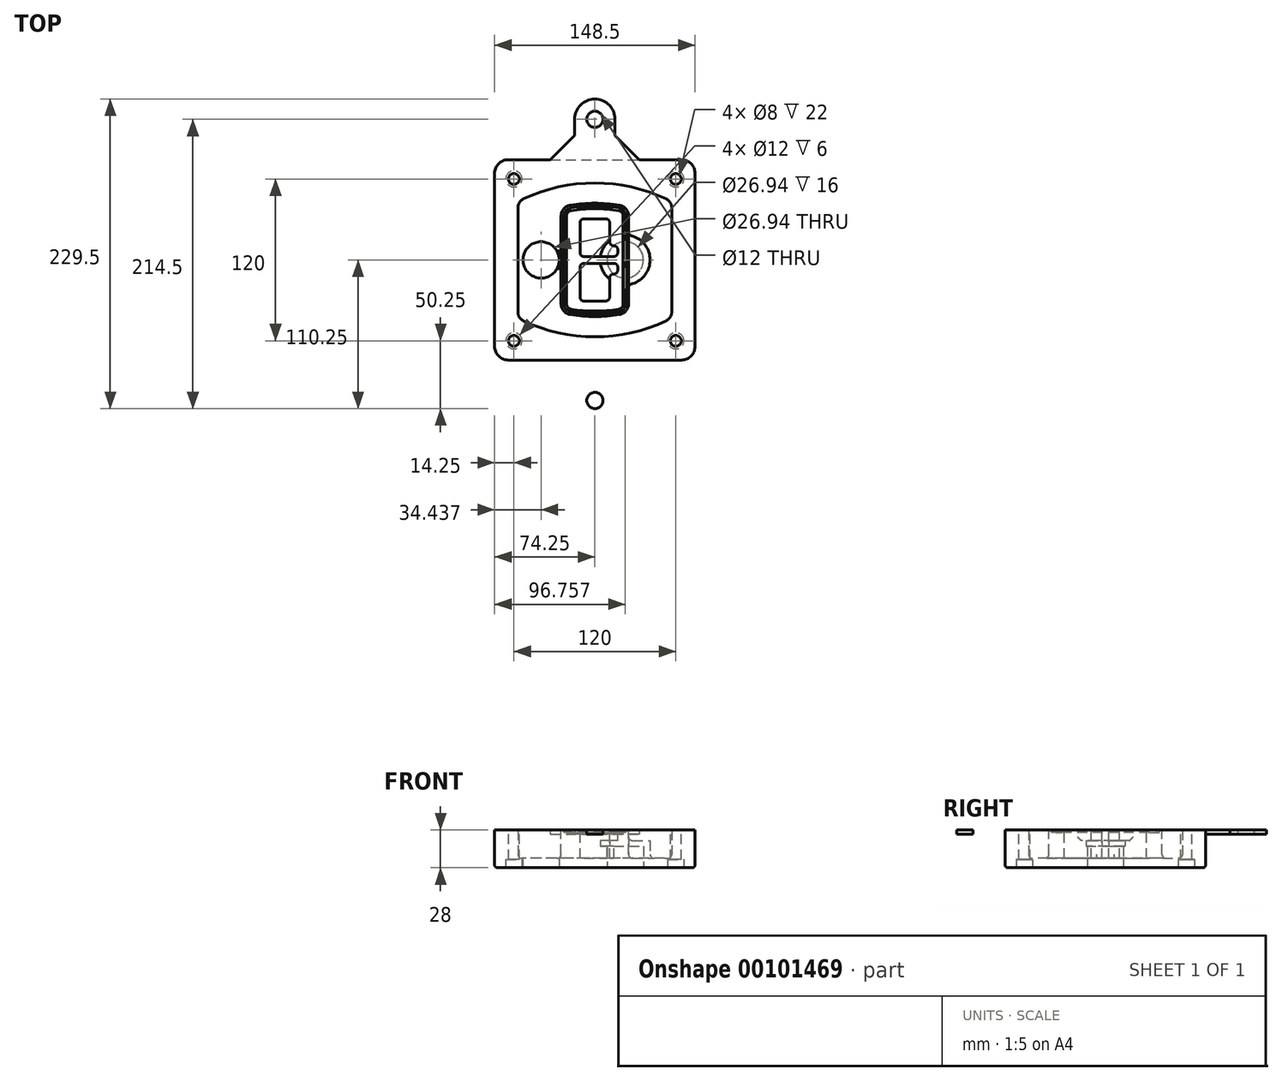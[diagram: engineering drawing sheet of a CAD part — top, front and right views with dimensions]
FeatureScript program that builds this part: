
annotation { "Feature Type Name" : "Feature", "Feature Type Description" : "" }
export const myFeature = defineFeature(function(context is Context, id is Id, definition is map)
    precondition{}
    {
        {
            var Q0;
            Q0=qCreatedBy(makeId("Top.planeOp"),FACE);
            var sketch = newSketch(context, id + "F0", { "sketchPlane" : qUnion([Q0])});
            skPoint(sketch, "E0.rect.middle", {"position": v(0, 0) * mm});
            skLineSegment(sketch, "E1.bottom", {"start": v(-64.25, -74.25) * mm, "end": v(64.25, -74.25) * mm});
            skLineSegment(sketch, "E1.top", {"start": v(-64.25, 74.25) * mm, "end": v(64.25, 74.25) * mm});
            skLineSegment(sketch, "E1.left", {"start": v(-74.25, -64.25) * mm, "end": v(-74.25, 64.25) * mm});
            skLineSegment(sketch, "E1.right", {"start": v(74.25, -64.25) * mm, "end": v(74.25, 64.25) * mm});
            skLineSegment(sketch, "E2", {"start": v(-74.25, 74.25) * mm, "end": v(74.25, -74.25) * mm, "construction": true});
            skLineSegment(sketch, "E3", {"start": v(74.25, 74.25) * mm, "end": v(-74.25, -74.25) * mm, "construction": true});
            skCircle(sketch, "E4", {"center": v(-60, 60) * mm, "radius": 4 * mm});
            skCircle(sketch, "E5", {"center": v(60, 60) * mm, "radius": 4 * mm});
            skCircle(sketch, "E6", {"center": v(60, -60) * mm, "radius": 4 * mm});
            skCircle(sketch, "E7", {"center": v(-60, -60) * mm, "radius": 4 * mm});
            skLineSegment(sketch, "E8", {"start": v(-60, 60) * mm, "end": v(60, 60) * mm, "construction": true});
            skLineSegment(sketch, "E9", {"start": v(60, 60) * mm, "end": v(60, -60) * mm, "construction": true});
            skLineSegment(sketch, "E10", {"start": v(60, -60) * mm, "end": v(-60, -60) * mm, "construction": true});
            skLineSegment(sketch, "E11", {"start": v(-60, -60) * mm, "end": v(-60, 60) * mm, "construction": true});
            skLineSegment(sketch, "E12", {"start": v(-60, 38.83) * mm, "end": v(-60, -38.83) * mm});
            skLineSegment(sketch, "E13", {"start": v(60, 38.83) * mm, "end": v(60, -38.83) * mm});
            skArc(sketch, "E14", {"start": v(54.26, 47.88) * mm, "mid": v(0, 60) * mm, "end": v(-54.26, 47.88) * mm});
            skArc(sketch, "E15", {"start": v(-54.26, -47.88) * mm, "mid": v(0, -60) * mm, "end": v(54.26, -47.88) * mm});
            skLineSegment(sketch, "E16", {"start": v(-60, 0) * mm, "end": v(60, 0) * mm, "construction": true});
            skPoint(sketch, "E17.visualSharp", {"position": v(-60, -45) * mm});
            skArc(sketch, "E17.filletArc", {"start": v(-60, -38.83) * mm, "mid": v(-58.44, -44.2) * mm, "end": v(-54.26, -47.88) * mm});
            skPoint(sketch, "E18.visualSharp", {"position": v(-60, 45) * mm});
            skArc(sketch, "E18.filletArc", {"start": v(-54.26, 47.88) * mm, "mid": v(-58.44, 44.2) * mm, "end": v(-60, 38.83) * mm});
            skPoint(sketch, "E19.visualSharp", {"position": v(60, 45) * mm});
            skArc(sketch, "E19.filletArc", {"start": v(60, 38.83) * mm, "mid": v(58.44, 44.2) * mm, "end": v(54.26, 47.88) * mm});
            skPoint(sketch, "E20.visualSharp", {"position": v(60, -45) * mm});
            skArc(sketch, "E20.filletArc", {"start": v(54.26, -47.88) * mm, "mid": v(58.44, -44.2) * mm, "end": v(60, -38.83) * mm});
            skPoint(sketch, "E21.visualSharp", {"position": v(-74.25, 74.25) * mm});
            skArc(sketch, "E21.filletArc", {"start": v(-64.25, 74.25) * mm, "mid": v(-71.32, 71.32) * mm, "end": v(-74.25, 64.25) * mm});
            skPoint(sketch, "E22.visualSharp", {"position": v(74.25, 74.25) * mm});
            skArc(sketch, "E22.filletArc", {"start": v(74.25, 64.25) * mm, "mid": v(71.32, 71.32) * mm, "end": v(64.25, 74.25) * mm});
            skPoint(sketch, "E23.visualSharp", {"position": v(74.25, -74.25) * mm});
            skArc(sketch, "E23.filletArc", {"start": v(64.25, -74.25) * mm, "mid": v(71.32, -71.32) * mm, "end": v(74.25, -64.25) * mm});
            skPoint(sketch, "E24.visualSharp", {"position": v(-74.25, -74.25) * mm});
            skArc(sketch, "E24.filletArc", {"start": v(-74.25, -64.25) * mm, "mid": v(-71.32, -71.32) * mm, "end": v(-64.25, -74.25) * mm});
            skArc(sketch, "E25.0", {"start": v(57, 38.83) * mm, "mid": v(55.9, 42.58) * mm, "end": v(52.98, 45.17) * mm});
            skLineSegment(sketch, "E25.1", {"start": v(57, 38.83) * mm, "end": v(57, -38.83) * mm});
            skArc(sketch, "E25.2", {"start": v(52.98, -45.17) * mm, "mid": v(55.9, -42.58) * mm, "end": v(57, -38.83) * mm});
            skArc(sketch, "E25.3", {"start": v(-52.98, -45.17) * mm, "mid": v(0, -57) * mm, "end": v(52.98, -45.17) * mm});
            skArc(sketch, "E25.4", {"start": v(-57, -38.83) * mm, "mid": v(-55.9, -42.58) * mm, "end": v(-52.98, -45.17) * mm});
            skArc(sketch, "E25.5", {"start": v(52.98, 45.17) * mm, "mid": v(0, 57) * mm, "end": v(-52.98, 45.17) * mm});
            skLineSegment(sketch, "E25.6", {"start": v(-57, 38.83) * mm, "end": v(-57, -38.83) * mm});
            skArc(sketch, "E25.7", {"start": v(-52.98, 45.17) * mm, "mid": v(-55.9, 42.58) * mm, "end": v(-57, 38.83) * mm});
            skArc(sketch, "E26.0", {"start": v(-55.96, 51.5) * mm, "mid": v(-61.82, 46.33) * mm, "end": v(-64, 38.83) * mm});
            skArc(sketch, "E26.1", {"start": v(55.96, 51.5) * mm, "mid": v(0, 64) * mm, "end": v(-55.96, 51.5) * mm});
            skArc(sketch, "E26.2", {"start": v(64, 38.83) * mm, "mid": v(61.82, 46.33) * mm, "end": v(55.96, 51.5) * mm});
            skLineSegment(sketch, "E26.3", {"start": v(64, 38.83) * mm, "end": v(64, -38.83) * mm});
            skArc(sketch, "E26.4", {"start": v(55.96, -51.5) * mm, "mid": v(61.82, -46.33) * mm, "end": v(64, -38.83) * mm});
            skLineSegment(sketch, "E26.5", {"start": v(-64, 38.83) * mm, "end": v(-64, -38.83) * mm});
            skArc(sketch, "E26.6", {"start": v(-55.96, -51.5) * mm, "mid": v(0, -64) * mm, "end": v(55.96, -51.5) * mm});
            skArc(sketch, "E26.7", {"start": v(-64, -38.83) * mm, "mid": v(-61.82, -46.33) * mm, "end": v(-55.96, -51.5) * mm});
            skSolve(sketch);
        }
        {
            var Q0;
            Q0=makeQuery(id+"F0.imprint","IMPRINT",FACE,{"disambiguationData":[TD([[makeQuery(id+"F0.imprint","IMPRINT",EDGE,{"derivedFrom":sQuery(id+"F0.wireOp",EDGE,"E1.bottom")}),1.0]])]});
            var Q1;
            Q1=makeQuery(id+"F0.imprint","IMPRINT",FACE,{"disambiguationData":[TD([[makeQuery(id+"F0.imprint","IMPRINT",EDGE,{"derivedFrom":sQuery(id+"F0.wireOp",EDGE,"E12")}),1.0]])]});
            var Q2;
            Q2=makeQuery(id+"F0.imprint","IMPRINT",FACE,{"disambiguationData":[TD([[makeQuery(id+"F0.imprint","IMPRINT",EDGE,{"derivedFrom":sQuery(id+"F0.wireOp",EDGE,"E25.0")}),1.0]])]});
            var Q3;
            Q3=makeQuery(id+"F0.imprint","IMPRINT",FACE,{"disambiguationData":[TD([[makeQuery(id+"F0.imprint","IMPRINT",EDGE,{"derivedFrom":sQuery(id+"F0.wireOp",EDGE,"E12")}),-1.0]])]});
            extrude(context, id + "F1", {"entities" : qUnion([Q0, Q1, Q2, Q3]), "oppositeDirection" : true, "depth" : 25 * mm});
        }
        {
            var Q0;
            Q0=makeQuery(id+"F0.imprint","IMPRINT",FACE,{"disambiguationData":[TD([[makeQuery(id+"F0.imprint","IMPRINT",EDGE,{"derivedFrom":sQuery(id+"F0.wireOp",EDGE,"E12")}),1.0]])]});
            extrude(context, id + "F2", {"entities" : qUnion([Q0]), "operationType" : NewBodyOperationType.ADD, "depth" : 3 * mm});
        }
        {
            var Q0;
            Q0=makeQuery(id+"F0.imprint","IMPRINT",FACE,{"disambiguationData":[TD([[makeQuery(id+"F0.imprint","IMPRINT",EDGE,{"derivedFrom":sQuery(id+"F0.wireOp",EDGE,"E25.0")}),1.0]])]});
            extrude(context, id + "F3", {"entities" : qUnion([Q0]), "operationType" : NewBodyOperationType.REMOVE, "oppositeDirection" : true, "depth" : 18 * mm});
        }
        {
            var Q0;
            Q0=makeQuery(id+"F2.opExtrude","CAP_FACE",FACE,{"disambiguationData":[OSD([sQuery(id+"F0.wireOp",EDGE,"E12"),sQuery(id+"F0.wireOp",EDGE,"E13"),sQuery(id+"F0.wireOp",EDGE,"E14"),sQuery(id+"F0.wireOp",EDGE,"E15"),sQuery(id+"F0.wireOp",EDGE,"E17.filletArc"),sQuery(id+"F0.wireOp",EDGE,"E18.filletArc"),sQuery(id+"F0.wireOp",EDGE,"E19.filletArc"),sQuery(id+"F0.wireOp",EDGE,"E20.filletArc"),sQuery(id+"F0.wireOp",EDGE,"E25.0"),sQuery(id+"F0.wireOp",EDGE,"E25.1"),sQuery(id+"F0.wireOp",EDGE,"E25.2"),sQuery(id+"F0.wireOp",EDGE,"E25.3"),sQuery(id+"F0.wireOp",EDGE,"E25.4"),sQuery(id+"F0.wireOp",EDGE,"E25.5"),sQuery(id+"F0.wireOp",EDGE,"E25.6"),sQuery(id+"F0.wireOp",EDGE,"E25.7")])],"isStart":false});
            var sketch = newSketch(context, id + "F4", { "sketchPlane" : qUnion([Q0])});
            skArc(sketch, "E27.0", {"start": v(-18.34, -40.45) * mm, "mid": v(0, -42) * mm, "end": v(18.34, -40.45) * mm});
            skArc(sketch, "E28.0", {"start": v(18.34, 40.45) * mm, "mid": v(0, 42) * mm, "end": v(-18.34, 40.45) * mm});
            skLineSegment(sketch, "E29", {"start": v(-25, 32.57) * mm, "end": v(-25, -32.57) * mm});
            skLineSegment(sketch, "E30", {"start": v(25, 32.57) * mm, "end": v(25, -32.57) * mm});
            skLineSegment(sketch, "E31", {"start": v(-25, 39.1) * mm, "end": v(25, 39.1) * mm, "construction": true});
            skLineSegment(sketch, "E32", {"start": v(-25, -39.1) * mm, "end": v(25, -39.1) * mm, "construction": true});
            skPoint(sketch, "E33.visualSharp", {"position": v(-25, 39.1) * mm});
            skArc(sketch, "E33.filletArc", {"start": v(-18.34, 40.45) * mm, "mid": v(-23.11, 37.73) * mm, "end": v(-25, 32.57) * mm});
            skPoint(sketch, "E34.visualSharp", {"position": v(25, 39.1) * mm});
            skArc(sketch, "E34.filletArc", {"start": v(25, 32.57) * mm, "mid": v(23.11, 37.73) * mm, "end": v(18.34, 40.45) * mm});
            skPoint(sketch, "E35.visualSharp", {"position": v(25, -39.1) * mm});
            skArc(sketch, "E35.filletArc", {"start": v(18.34, -40.45) * mm, "mid": v(23.11, -37.73) * mm, "end": v(25, -32.57) * mm});
            skPoint(sketch, "E36.visualSharp", {"position": v(-25, -39.1) * mm});
            skArc(sketch, "E36.filletArc", {"start": v(-25, -32.57) * mm, "mid": v(-23.11, -37.73) * mm, "end": v(-18.34, -40.45) * mm});
            skArc(sketch, "E37.0", {"start": v(52.98, 45.17) * mm, "mid": v(0, 57) * mm, "end": v(-52.98, 45.17) * mm});
            skArc(sketch, "E37.1", {"start": v(-52.98, 45.17) * mm, "mid": v(-55.9, 42.58) * mm, "end": v(-57, 38.83) * mm});
            skLineSegment(sketch, "E37.2", {"start": v(-57, 38.83) * mm, "end": v(-57, -38.83) * mm});
            skArc(sketch, "E37.3", {"start": v(-57, -38.83) * mm, "mid": v(-55.9, -42.58) * mm, "end": v(-52.98, -45.17) * mm});
            skArc(sketch, "E37.4", {"start": v(-52.98, -45.17) * mm, "mid": v(0, -57) * mm, "end": v(52.98, -45.17) * mm});
            skArc(sketch, "E37.5", {"start": v(52.98, -45.17) * mm, "mid": v(55.9, -42.58) * mm, "end": v(57, -38.83) * mm});
            skLineSegment(sketch, "E37.6", {"start": v(57, 38.83) * mm, "end": v(57, -38.83) * mm});
            skArc(sketch, "E37.7", {"start": v(57, 38.83) * mm, "mid": v(55.9, 42.58) * mm, "end": v(52.98, 45.17) * mm});
            skLineSegment(sketch, "E38.0", {"start": v(23, 32.57) * mm, "end": v(23, -32.57) * mm});
            skArc(sketch, "E38.1", {"start": v(18, -38.48) * mm, "mid": v(21.58, -36.44) * mm, "end": v(23, -32.57) * mm});
            skArc(sketch, "E38.2", {"start": v(-18, -38.48) * mm, "mid": v(0, -40) * mm, "end": v(18, -38.48) * mm});
            skArc(sketch, "E38.3", {"start": v(-23, -32.57) * mm, "mid": v(-21.58, -36.44) * mm, "end": v(-18, -38.48) * mm});
            skLineSegment(sketch, "E38.4", {"start": v(-23, 32.57) * mm, "end": v(-23, -32.57) * mm});
            skArc(sketch, "E38.5", {"start": v(23, 32.57) * mm, "mid": v(21.58, 36.44) * mm, "end": v(18, 38.48) * mm});
            skArc(sketch, "E38.6", {"start": v(-18, 38.48) * mm, "mid": v(-21.58, 36.44) * mm, "end": v(-23, 32.57) * mm});
            skArc(sketch, "E38.7", {"start": v(18, 38.48) * mm, "mid": v(0, 40) * mm, "end": v(-18, 38.48) * mm});
            skArc(sketch, "E39.0", {"start": v(21, 32.57) * mm, "mid": v(20.06, 35.15) * mm, "end": v(17.67, 36.5) * mm});
            skLineSegment(sketch, "E39.1", {"start": v(21, 32.57) * mm, "end": v(21, -32.57) * mm});
            skArc(sketch, "E39.2", {"start": v(17.67, -36.5) * mm, "mid": v(20.06, -35.15) * mm, "end": v(21, -32.57) * mm});
            skArc(sketch, "E39.3", {"start": v(-17.67, -36.5) * mm, "mid": v(0, -38) * mm, "end": v(17.67, -36.5) * mm});
            skArc(sketch, "E39.4", {"start": v(-21, -32.57) * mm, "mid": v(-20.06, -35.15) * mm, "end": v(-17.67, -36.5) * mm});
            skArc(sketch, "E39.5", {"start": v(17.67, 36.5) * mm, "mid": v(0, 38) * mm, "end": v(-17.67, 36.5) * mm});
            skLineSegment(sketch, "E39.6", {"start": v(-21, 32.57) * mm, "end": v(-21, -32.57) * mm});
            skArc(sketch, "E39.7", {"start": v(-17.67, 36.5) * mm, "mid": v(-20.06, 35.15) * mm, "end": v(-21, 32.57) * mm});
            skLineSegment(sketch, "E40", {"start": v(-25, 0) * mm, "end": v(25, 0) * mm, "construction": true});
            skLineSegment(sketch, "E41", {"start": v(-11, 5.5) * mm, "end": v(-11, 27.5) * mm});
            skLineSegment(sketch, "E42", {"start": v(-8, 30.5) * mm, "end": v(8, 30.5) * mm});
            skLineSegment(sketch, "E43", {"start": v(11, 27.5) * mm, "end": v(11, 13.5) * mm});
            skLineSegment(sketch, "E44", {"start": v(14, 10.5) * mm, "end": v(14, 10.5) * mm});
            skLineSegment(sketch, "E45", {"start": v(17, 7.5) * mm, "end": v(17, 5.5) * mm});
            skLineSegment(sketch, "E46", {"start": v(14, 2.5) * mm, "end": v(-8, 2.5) * mm});
            skPoint(sketch, "E47.visualSharp", {"position": v(-11, 30.5) * mm});
            skArc(sketch, "E47.filletArc", {"start": v(-8, 30.5) * mm, "mid": v(-10.12, 29.62) * mm, "end": v(-11, 27.5) * mm});
            skPoint(sketch, "E48.visualSharp", {"position": v(11, 30.5) * mm});
            skArc(sketch, "E48.filletArc", {"start": v(11, 27.5) * mm, "mid": v(10.12, 29.62) * mm, "end": v(8, 30.5) * mm});
            skPoint(sketch, "E49.visualSharp", {"position": v(11, 10.5) * mm});
            skArc(sketch, "E49.filletArc", {"start": v(11, 13.5) * mm, "mid": v(11.88, 11.38) * mm, "end": v(14, 10.5) * mm});
            skPoint(sketch, "E50.visualSharp", {"position": v(17, 10.5) * mm});
            skArc(sketch, "E50.filletArc", {"start": v(17, 7.5) * mm, "mid": v(16.12, 9.62) * mm, "end": v(14, 10.5) * mm});
            skPoint(sketch, "E51.visualSharp", {"position": v(17, 2.5) * mm});
            skArc(sketch, "E51.filletArc", {"start": v(14, 2.5) * mm, "mid": v(16.12, 3.38) * mm, "end": v(17, 5.5) * mm});
            skPoint(sketch, "E52.visualSharp", {"position": v(-11, 2.5) * mm});
            skArc(sketch, "E52.filletArc", {"start": v(-11, 5.5) * mm, "mid": v(-10.12, 3.38) * mm, "end": v(-8, 2.5) * mm});
            skLineSegment(sketch, "E53.0.MirrorCS", {"start": v(14, -2.5) * mm, "end": v(-8, -2.5) * mm});
            skArc(sketch, "E54.0.MirrorCS", {"start": v(-11, -5.5) * mm, "mid": v(-10.12, -3.38) * mm, "end": v(-8, -2.5) * mm});
            skLineSegment(sketch, "E55.0.MirrorCS", {"start": v(-11, -5.5) * mm, "end": v(-11, -27.5) * mm});
            skArc(sketch, "E56.0.MirrorCS", {"start": v(-8, -30.5) * mm, "mid": v(-10.12, -29.62) * mm, "end": v(-11, -27.5) * mm});
            skLineSegment(sketch, "E57.0.MirrorCS", {"start": v(-8, -30.5) * mm, "end": v(8, -30.5) * mm});
            skArc(sketch, "E58.0.MirrorCS", {"start": v(11, -27.5) * mm, "mid": v(10.12, -29.62) * mm, "end": v(8, -30.5) * mm});
            skLineSegment(sketch, "E59.0.MirrorCS", {"start": v(11, -27.5) * mm, "end": v(11, -13.5) * mm});
            skArc(sketch, "E60.0.MirrorCS", {"start": v(11, -13.5) * mm, "mid": v(11.88, -11.38) * mm, "end": v(14, -10.5) * mm});
            skArc(sketch, "E61.0.MirrorCS", {"start": v(17, -7.5) * mm, "mid": v(16.12, -9.62) * mm, "end": v(14, -10.5) * mm});
            skLineSegment(sketch, "E62.0.MirrorCS", {"start": v(17, -7.5) * mm, "end": v(17, -5.5) * mm});
            skArc(sketch, "E63.0.MirrorCS", {"start": v(14, -2.5) * mm, "mid": v(16.12, -3.38) * mm, "end": v(17, -5.5) * mm});
            skSolve(sketch);
        }
        {
            var Q0;
            Q0=makeQuery(id+"F4.imprint","IMPRINT",FACE,{"disambiguationData":[TD([[makeQuery(id+"F4.imprint","IMPRINT",EDGE,{"derivedFrom":sQuery(id+"F4.wireOp",EDGE,"E27.0")}),1.0]])]});
            var Q1;
            Q1=makeQuery(id+"F4.imprint","IMPRINT",FACE,{"disambiguationData":[TD([[makeQuery(id+"F4.imprint","IMPRINT",EDGE,{"derivedFrom":sQuery(id+"F4.wireOp",EDGE,"E38.0")}),-1.0]])]});
            var Q2;
            Q2=makeQuery(id+"F4.imprint","IMPRINT",FACE,{"disambiguationData":[TD([[makeQuery(id+"F4.imprint","IMPRINT",EDGE,{"derivedFrom":sQuery(id+"F4.wireOp",EDGE,"E39.0")}),1.0]])]});
            extrude(context, id + "F5", {"entities" : qUnion([Q0, Q1, Q2]), "operationType" : NewBodyOperationType.ADD, "endBound" : BoundingType.UP_TO_NEXT, "oppositeDirection" : true, "depth" : 25 * mm});
        }
        {
            var Q0;
            Q0=makeQuery(id+"F4.imprint","IMPRINT",FACE,{"disambiguationData":[TD([[makeQuery(id+"F4.imprint","IMPRINT",EDGE,{"derivedFrom":sQuery(id+"F4.wireOp",EDGE,"E38.0")}),-1.0]])]});
            extrude(context, id + "F6", {"entities" : qUnion([Q0]), "operationType" : NewBodyOperationType.REMOVE, "oppositeDirection" : true, "depth" : 2 * mm});
        }
        {
            var Q0;
            Q0=makeQuery(id+"F1.opExtrude","CAP_FACE",FACE,{"disambiguationData":[OSD([sQuery(id+"F0.wireOp",EDGE,"E1.bottom"),sQuery(id+"F0.wireOp",EDGE,"E1.top"),sQuery(id+"F0.wireOp",EDGE,"E1.left"),sQuery(id+"F0.wireOp",EDGE,"E1.right"),sQuery(id+"F0.wireOp",EDGE,"E4"),sQuery(id+"F0.wireOp",EDGE,"E5"),sQuery(id+"F0.wireOp",EDGE,"E6"),sQuery(id+"F0.wireOp",EDGE,"E7"),sQuery(id+"F0.wireOp",EDGE,"E21.filletArc"),sQuery(id+"F0.wireOp",EDGE,"E22.filletArc"),sQuery(id+"F0.wireOp",EDGE,"E23.filletArc"),sQuery(id+"F0.wireOp",EDGE,"E24.filletArc")])],"isStart":false});
            var sketch = newSketch(context, id + "F7", { "sketchPlane" : qUnion([Q0])});
            skCircle(sketch, "E64", {"center": v(22.5, 0) * mm, "radius": 13.47 * mm});
            skCircle(sketch, "E65", {"center": v(-39.81, 0) * mm, "radius": 13.47 * mm});
            skLineSegment(sketch, "E66", {"start": v(74.25, 0) * mm, "end": v(-74.25, 0) * mm});
            skCircle(sketch, "E67", {"center": v(22.5, 0) * mm, "radius": 18.47 * mm});
            skCircle(sketch, "E68", {"center": v(60, -60) * mm, "radius": 6 * mm});
            skCircle(sketch, "E69", {"center": v(-60, -60) * mm, "radius": 6 * mm});
            skCircle(sketch, "E70", {"center": v(-60, 60) * mm, "radius": 6 * mm});
            skCircle(sketch, "E71", {"center": v(60, 60) * mm, "radius": 6 * mm});
            skSolve(sketch);
        }
        {
            var Q0;
            {var subQ1=sQuery(id+"F7.wireOp",EDGE,"E66");var subQ4=sQuery(id+"F7.wireOp",EDGE,"E64");var subQ6=makeQuery(id+"F7.imprint","INTERSECT",VERTEX,{"disambiguationData":[OD(0.0)],"derivedFrom":[subQ4,subQ1]});Q0=makeQuery(id+"F7.imprint","IMPRINT",FACE,{"disambiguationData":[TD([[makeQuery(id+"F7.imprint","IMPRINT",EDGE,{"disambiguationData":[TD([[subQ6,-1.0]])],"derivedFrom":subQ4}),-1.0]])]});}
            var Q1;
            {var subQ0=sQuery(id+"F7.wireOp",EDGE,"E66");var subQ1=sQuery(id+"F7.wireOp",EDGE,"E64");var subQ3=makeQuery(id+"F7.imprint","INTERSECT",VERTEX,{"disambiguationData":[OD(0.0)],"derivedFrom":[subQ1,subQ0]});Q1=makeQuery(id+"F7.imprint","IMPRINT",FACE,{"disambiguationData":[TD([[makeQuery(id+"F7.imprint","IMPRINT",EDGE,{"disambiguationData":[TD([[subQ3,-1.0]])],"derivedFrom":subQ1}),1.0]])]});}
            var Q2;
            {var subQ0=sQuery(id+"F7.wireOp",EDGE,"E66");var subQ1=sQuery(id+"F7.wireOp",EDGE,"E64");var subQ3=makeQuery(id+"F7.imprint","INTERSECT",VERTEX,{"disambiguationData":[OD(0.0)],"derivedFrom":[subQ1,subQ0]});Q2=makeQuery(id+"F7.imprint","IMPRINT",FACE,{"disambiguationData":[TD([[makeQuery(id+"F7.imprint","IMPRINT",EDGE,{"disambiguationData":[TD([[subQ3,1.0]])],"derivedFrom":subQ1}),1.0]])]});}
            var Q3;
            {var subQ1=sQuery(id+"F7.wireOp",EDGE,"E66");var subQ4=sQuery(id+"F7.wireOp",EDGE,"E64");var subQ6=makeQuery(id+"F7.imprint","INTERSECT",VERTEX,{"disambiguationData":[OD(0.0)],"derivedFrom":[subQ4,subQ1]});Q3=makeQuery(id+"F7.imprint","IMPRINT",FACE,{"disambiguationData":[TD([[makeQuery(id+"F7.imprint","IMPRINT",EDGE,{"disambiguationData":[TD([[subQ6,1.0]])],"derivedFrom":subQ4}),-1.0]])]});}
            extrude(context, id + "F8", {"entities" : qUnion([Q0, Q1, Q2, Q3]), "operationType" : NewBodyOperationType.ADD, "oppositeDirection" : true, "depth" : 20 * mm});
        }
        {
            var Q0;
            {var subQ0=sQuery(id+"F7.wireOp",EDGE,"E66");var subQ1=sQuery(id+"F7.wireOp",EDGE,"E64");var subQ3=makeQuery(id+"F7.imprint","INTERSECT",VERTEX,{"disambiguationData":[OD(0.0)],"derivedFrom":[subQ1,subQ0]});Q0=makeQuery(id+"F7.imprint","IMPRINT",FACE,{"disambiguationData":[TD([[makeQuery(id+"F7.imprint","IMPRINT",EDGE,{"disambiguationData":[TD([[subQ3,-1.0]])],"derivedFrom":subQ1}),1.0]])]});}
            var Q1;
            {var subQ0=sQuery(id+"F7.wireOp",EDGE,"E66");var subQ1=sQuery(id+"F7.wireOp",EDGE,"E64");var subQ3=makeQuery(id+"F7.imprint","INTERSECT",VERTEX,{"disambiguationData":[OD(0.0)],"derivedFrom":[subQ1,subQ0]});Q1=makeQuery(id+"F7.imprint","IMPRINT",FACE,{"disambiguationData":[TD([[makeQuery(id+"F7.imprint","IMPRINT",EDGE,{"disambiguationData":[TD([[subQ3,1.0]])],"derivedFrom":subQ1}),1.0]])]});}
            extrude(context, id + "F9", {"entities" : qUnion([Q0, Q1]), "operationType" : NewBodyOperationType.REMOVE, "oppositeDirection" : true, "depth" : 16 * mm});
        }
        {
            var Q0;
            {var subQ0=sQuery(id+"F7.wireOp",EDGE,"E66");var subQ1=sQuery(id+"F7.wireOp",EDGE,"E65");var subQ3=makeQuery(id+"F7.imprint","INTERSECT",VERTEX,{"disambiguationData":[OD(0.0)],"derivedFrom":[subQ1,subQ0]});Q0=makeQuery(id+"F7.imprint","IMPRINT",FACE,{"disambiguationData":[TD([[makeQuery(id+"F7.imprint","IMPRINT",EDGE,{"disambiguationData":[TD([[subQ3,-1.0]])],"derivedFrom":subQ1}),1.0]])]});}
            var Q1;
            {var subQ0=sQuery(id+"F7.wireOp",EDGE,"E66");var subQ1=sQuery(id+"F7.wireOp",EDGE,"E65");var subQ3=makeQuery(id+"F7.imprint","INTERSECT",VERTEX,{"disambiguationData":[OD(0.0)],"derivedFrom":[subQ1,subQ0]});Q1=makeQuery(id+"F7.imprint","IMPRINT",FACE,{"disambiguationData":[TD([[makeQuery(id+"F7.imprint","IMPRINT",EDGE,{"disambiguationData":[TD([[subQ3,1.0]])],"derivedFrom":subQ1}),1.0]])]});}
            extrude(context, id + "F10", {"entities" : qUnion([Q0, Q1]), "operationType" : NewBodyOperationType.REMOVE, "oppositeDirection" : true, "depth" : 25 * mm});
        }
        {
            var Q0;
            Q0=makeQuery(id+"F7.imprint","IMPRINT",FACE,{"disambiguationData":[TD([[makeQuery(id+"F7.imprint","IMPRINT",EDGE,{"derivedFrom":sQuery(id+"F7.wireOp",EDGE,"E68")}),1.0]])]});
            var Q1;
            Q1=makeQuery(id+"F7.imprint","IMPRINT",FACE,{"disambiguationData":[TD([[makeQuery(id+"F7.imprint","IMPRINT",EDGE,{"derivedFrom":makeQuery(id+"F1.opExtrude","CAP_EDGE",EDGE,{"disambiguationData":[OSD([sQuery(id+"F0.wireOp",EDGE,"E5")])],"isStart":false})}),-1.0]])]});
            var Q2;
            Q2=makeQuery(id+"F7.imprint","IMPRINT",FACE,{"disambiguationData":[TD([[makeQuery(id+"F7.imprint","IMPRINT",EDGE,{"derivedFrom":sQuery(id+"F7.wireOp",EDGE,"E69")}),1.0]])]});
            var Q3;
            Q3=makeQuery(id+"F7.imprint","IMPRINT",FACE,{"disambiguationData":[TD([[makeQuery(id+"F7.imprint","IMPRINT",EDGE,{"derivedFrom":makeQuery(id+"F1.opExtrude","CAP_EDGE",EDGE,{"disambiguationData":[OSD([sQuery(id+"F0.wireOp",EDGE,"E4")])],"isStart":false})}),-1.0]])]});
            var Q4;
            Q4=makeQuery(id+"F7.imprint","IMPRINT",FACE,{"disambiguationData":[TD([[makeQuery(id+"F7.imprint","IMPRINT",EDGE,{"derivedFrom":sQuery(id+"F7.wireOp",EDGE,"E70")}),1.0]])]});
            var Q5;
            Q5=makeQuery(id+"F7.imprint","IMPRINT",FACE,{"disambiguationData":[TD([[makeQuery(id+"F7.imprint","IMPRINT",EDGE,{"derivedFrom":makeQuery(id+"F1.opExtrude","CAP_EDGE",EDGE,{"disambiguationData":[OSD([sQuery(id+"F0.wireOp",EDGE,"E7")])],"isStart":false})}),-1.0]])]});
            var Q6;
            Q6=makeQuery(id+"F7.imprint","IMPRINT",FACE,{"disambiguationData":[TD([[makeQuery(id+"F7.imprint","IMPRINT",EDGE,{"derivedFrom":sQuery(id+"F7.wireOp",EDGE,"E71")}),1.0]])]});
            var Q7;
            Q7=makeQuery(id+"F7.imprint","IMPRINT",FACE,{"disambiguationData":[TD([[makeQuery(id+"F7.imprint","IMPRINT",EDGE,{"derivedFrom":makeQuery(id+"F1.opExtrude","CAP_EDGE",EDGE,{"disambiguationData":[OSD([sQuery(id+"F0.wireOp",EDGE,"E6")])],"isStart":false})}),-1.0]])]});
            extrude(context, id + "F11", {"entities" : qUnion([Q0, Q1, Q2, Q3, Q4, Q5, Q6, Q7]), "operationType" : NewBodyOperationType.REMOVE, "oppositeDirection" : true, "depth" : 6 * mm});
        }
        {
            var Q0;
            Q0=makeQuery(id+"F9.boolean.opBoolean","COPY",FACE,{"derivedFrom":makeQuery(id+"F9.opExtrude","CAP_FACE",FACE,{"disambiguationData":[OSD([sQuery(id+"F7.wireOp",EDGE,"E64")])],"isStart":false})});
            var sketch = newSketch(context, id + "F12", { "sketchPlane" : qUnion([Q0])});
            skArc(sketch, "E72.0", {"start": v(11, 14.45) * mm, "mid": v(6.45, 9.13) * mm, "end": v(4.2, 2.5) * mm});
            skArc(sketch, "E72.1", {"start": v(4.2, -2.5) * mm, "mid": v(6.45, -9.13) * mm, "end": v(11, -14.45) * mm});
            skLineSegment(sketch, "E73", {"start": v(4.2, -2.5) * mm, "end": v(14, -2.5) * mm});
            skLineSegment(sketch, "E74.0", {"start": v(14, 2.5) * mm, "end": v(4.2, 2.5) * mm});
            skArc(sketch, "E74.1", {"start": v(14, 2.5) * mm, "mid": v(16.12, 3.38) * mm, "end": v(17, 5.5) * mm});
            skLineSegment(sketch, "E74.2", {"start": v(17, 7.5) * mm, "end": v(17, 5.5) * mm});
            skArc(sketch, "E74.3", {"start": v(17, 7.5) * mm, "mid": v(16.12, 9.62) * mm, "end": v(14, 10.5) * mm});
            skArc(sketch, "E74.4", {"start": v(11, 13.5) * mm, "mid": v(11.88, 11.38) * mm, "end": v(14, 10.5) * mm});
            skLineSegment(sketch, "E74.5", {"start": v(11, 14.45) * mm, "end": v(11, 13.5) * mm});
            skLineSegment(sketch, "E74.7", {"start": v(14, -2.5) * mm, "end": v(4.2, -2.5) * mm});
            skArc(sketch, "E74.8", {"start": v(14, -2.5) * mm, "mid": v(16.12, -3.38) * mm, "end": v(17, -5.5) * mm});
            skLineSegment(sketch, "E74.9", {"start": v(17, -7.5) * mm, "end": v(17, -5.5) * mm});
            skArc(sketch, "E74.10", {"start": v(17, -7.5) * mm, "mid": v(16.12, -9.62) * mm, "end": v(14, -10.5) * mm});
            skArc(sketch, "E74.11", {"start": v(11, -13.5) * mm, "mid": v(11.88, -11.38) * mm, "end": v(14, -10.5) * mm});
            skLineSegment(sketch, "E74.12", {"start": v(11, -14.45) * mm, "end": v(11, -13.5) * mm});
            skPoint(sketch, "E75.orphan", {"position": v(11, -27.5) * mm});
            skPoint(sketch, "E76.orphan", {"position": v(-8, -2.5) * mm});
            skPoint(sketch, "E77.orphan", {"position": v(-8, 2.5) * mm});
            skPoint(sketch, "E78.orphan", {"position": v(11, 27.5) * mm});
            skSolve(sketch);
        }
        {
            var Q0;
            {var subQ7=sQuery(id+"F12.wireOp",EDGE,"E72.0");var subQ14=sQuery(id+"F12.wireOp",EDGE,"E72.1");var subQ16=sQuery(id+"F12.wireOp",EDGE,"E74.1");var subQ18=sQuery(id+"F12.wireOp",EDGE,"E74.8");Q0=qUnion([makeQuery(id+"F12.imprint","IMPRINT",FACE,{"disambiguationData":[TD([[makeQuery(id+"F12.imprint","IMPRINT",EDGE,{"derivedFrom":subQ7}),1.0]])]}),makeQuery(id+"F12.imprint","IMPRINT",FACE,{"disambiguationData":[TD([[makeQuery(id+"F12.imprint","IMPRINT",EDGE,{"derivedFrom":subQ14}),1.0]])]}),makeQuery(id+"F12.imprint","IMPRINT",FACE,{"disambiguationData":[TD([[makeQuery(id+"F12.imprint","IMPRINT",EDGE,{"derivedFrom":subQ16}),1.0]])]}),makeQuery(id+"F12.imprint","IMPRINT",FACE,{"disambiguationData":[TD([[makeQuery(id+"F12.imprint","IMPRINT",EDGE,{"derivedFrom":subQ18}),-1.0]])]})]);}
            var Q1;
            Q1=makeQuery(id+"F5.boolean.opBoolean","SPLIT",FACE,{"disambiguationData":[TD([makeQuery(id+"F5.opExtrude","SWEPT_FACE",FACE,{"disambiguationData":[OSD([sQuery(id+"F4.wireOp",EDGE,"E41")])]})])],"derivedFrom":makeQuery(id+"F3.boolean.opBoolean","COPY",FACE,{"derivedFrom":makeQuery(id+"F3.opExtrude","CAP_FACE",FACE,{"disambiguationData":[OSD([sQuery(id+"F0.wireOp",EDGE,"E25.0"),sQuery(id+"F0.wireOp",EDGE,"E25.1"),sQuery(id+"F0.wireOp",EDGE,"E25.2"),sQuery(id+"F0.wireOp",EDGE,"E25.3"),sQuery(id+"F0.wireOp",EDGE,"E25.4"),sQuery(id+"F0.wireOp",EDGE,"E25.5"),sQuery(id+"F0.wireOp",EDGE,"E25.6"),sQuery(id+"F0.wireOp",EDGE,"E25.7")])],"isStart":false})})});
            extrude(context, id + "F13", {"entities" : qUnion([Q0]), "operationType" : NewBodyOperationType.REMOVE, "endBound" : BoundingType.UP_TO_SURFACE, "endBoundEntityFace" : qUnion([Q1]), "depth" : 25 * mm});
        }
        {
            var Q0;
            Q0=makeQuery(id+"F3.boolean.opBoolean","COPY",EDGE,{"derivedFrom":makeQuery(id+"F3.opExtrude","CAP_EDGE",EDGE,{"disambiguationData":[OSD([sQuery(id+"F0.wireOp",EDGE,"E25.6")])],"isStart":false})});
            var Q1;
            Q1=makeQuery(id+"F8.boolean.opBoolean","INTERSECT",EDGE,{"derivedFrom":[makeQuery(id+"F5.opExtrude","SWEPT_FACE",FACE,{"disambiguationData":[OSD([sQuery(id+"F4.wireOp",EDGE,"E30")])]}),makeQuery(id+"F8.opExtrude","CAP_FACE",FACE,{"disambiguationData":[OSD([sQuery(id+"F7.wireOp",EDGE,"E67")])],"isStart":false})]});
            var Q2;
            Q2=makeQuery(id+"F8.boolean.opBoolean","INTERSECT",EDGE,{"disambiguationData":[OD(1.0)],"derivedFrom":[makeQuery(id+"F5.opExtrude","SWEPT_FACE",FACE,{"disambiguationData":[OSD([sQuery(id+"F4.wireOp",EDGE,"E30")])]}),makeQuery(id+"F8.opExtrude","SWEPT_FACE",FACE,{"disambiguationData":[OSD([sQuery(id+"F7.wireOp",EDGE,"E67")])]})]});
            var Q3;
            {var subQ0=sQuery(id+"F4.wireOp",EDGE,"E30");Q3=makeQuery(id+"F8.boolean.opBoolean","SPLIT",EDGE,{"disambiguationData":[TD([makeQuery(id+"F5.opExtrude","SWEPT_FACE",FACE,{"disambiguationData":[OSD([sQuery(id+"F4.wireOp",EDGE,"E35.filletArc")])]})])],"derivedFrom":makeQuery(id+"F5.opExtrude","CAP_EDGE",EDGE,{"disambiguationData":[OSD([subQ0])],"isStart":false})});}
            var Q4;
            {var subQ0=sQuery(id+"F0.wireOp",EDGE,"E25.7");var subQ1=sQuery(id+"F0.wireOp",EDGE,"E25.1");var subQ2=sQuery(id+"F0.wireOp",EDGE,"E25.6");var subQ3=sQuery(id+"F0.wireOp",EDGE,"E25.5");var subQ4=sQuery(id+"F0.wireOp",EDGE,"E25.4");var subQ5=sQuery(id+"F0.wireOp",EDGE,"E25.0");var subQ6=sQuery(id+"F0.wireOp",EDGE,"E25.2");var subQ7=sQuery(id+"F0.wireOp",EDGE,"E25.3");Q4=makeQuery(id+"F8.boolean.opBoolean","INTERSECT",EDGE,{"derivedFrom":[makeQuery(id+"F5.boolean.opBoolean","SPLIT",FACE,{"disambiguationData":[TD([makeQuery(id+"F2.opExtrude","SWEPT_FACE",FACE,{"disambiguationData":[OSD([subQ5])]})])],"derivedFrom":makeQuery(id+"F3.boolean.opBoolean","COPY",FACE,{"derivedFrom":makeQuery(id+"F3.opExtrude","CAP_FACE",FACE,{"disambiguationData":[OSD([subQ5,subQ1,subQ6,subQ7,subQ4,subQ3,subQ2,subQ0])],"isStart":false})})}),makeQuery(id+"F8.opExtrude","SWEPT_FACE",FACE,{"disambiguationData":[OSD([sQuery(id+"F7.wireOp",EDGE,"E67")])]})]});}
            var Q5;
            Q5=makeQuery(id+"F8.boolean.opBoolean","INTERSECT",EDGE,{"disambiguationData":[OD(0.0)],"derivedFrom":[makeQuery(id+"F5.opExtrude","SWEPT_FACE",FACE,{"disambiguationData":[OSD([sQuery(id+"F4.wireOp",EDGE,"E30")])]}),makeQuery(id+"F8.opExtrude","SWEPT_FACE",FACE,{"disambiguationData":[OSD([sQuery(id+"F7.wireOp",EDGE,"E67")])]})]});
            fillet(context, id + "F14", {"entities" : qUnion([Q0, Q1, Q2, Q3, Q4, Q5]), "radius" : 3 * mm, "tangentPropagation" : true, "allowEdgeOverflow" : false});
        }
        {
            var Q0;
            Q0=makeQuery(id+"F1.opExtrude","CAP_EDGE",EDGE,{"disambiguationData":[OSD([sQuery(id+"F0.wireOp",EDGE,"E1.bottom")])],"isStart":false});
            fillet(context, id + "F15", {"entities" : qUnion([Q0]), "radius" : 2 * mm, "tangentPropagation" : true, "allowEdgeOverflow" : false});
        }
        {
            var Q0;
            {var subQ0=sQuery(id+"F0.wireOp",EDGE,"E22.filletArc");var subQ1=sQuery(id+"F0.wireOp",EDGE,"E7");var subQ2=sQuery(id+"F0.wireOp",EDGE,"E6");var subQ3=sQuery(id+"F0.wireOp",EDGE,"E5");var subQ4=sQuery(id+"F0.wireOp",EDGE,"E4");var subQ5=sQuery(id+"F0.wireOp",EDGE,"E1.bottom");var subQ6=sQuery(id+"F0.wireOp",EDGE,"E21.filletArc");var subQ7=sQuery(id+"F0.wireOp",EDGE,"E1.top");var subQ8=sQuery(id+"F0.wireOp",EDGE,"E1.left");var subQ9=sQuery(id+"F0.wireOp",EDGE,"E1.right");var subQ10=sQuery(id+"F0.wireOp",EDGE,"E23.filletArc");var subQ11=sQuery(id+"F0.wireOp",EDGE,"E24.filletArc");Q0=makeQuery(id+"F2.boolean.opBoolean","SPLIT",FACE,{"disambiguationData":[TD([makeQuery(id+"F1.opExtrude","SWEPT_FACE",FACE,{"disambiguationData":[OSD([subQ5])]})])],"derivedFrom":makeQuery(id+"F1.opExtrude","CAP_FACE",FACE,{"disambiguationData":[OSD([subQ5,subQ7,subQ8,subQ9,subQ4,subQ3,subQ2,subQ1,subQ6,subQ0,subQ10,subQ11])],"isStart":true})});}
            var sketch = newSketch(context, id + "F16", { "sketchPlane" : qUnion([Q0])});
            skLineSegment(sketch, "E79", {"start": v(0, 74.25) * mm, "end": v(0, 104.25) * mm, "construction": true});
            skPoint(sketch, "E79.endSnap0", {"position": v(0, 74.25) * mm});
            skCircle(sketch, "E80", {"center": v(0, 104.25) * mm, "radius": 6 * mm});
            skLineSegment(sketch, "E81", {"start": v(-33, 74.25) * mm, "end": v(-15, 92.25) * mm});
            skLineSegment(sketch, "E82", {"start": v(-15, 92.25) * mm, "end": v(-15, 104.25) * mm});
            skLineSegment(sketch, "E83", {"start": v(33, 74.25) * mm, "end": v(15, 92.25) * mm});
            skLineSegment(sketch, "E84", {"start": v(15, 92.25) * mm, "end": v(15, 104.25) * mm});
            skArc(sketch, "E85", {"start": v(15, 104.25) * mm, "mid": v(0, 119.25) * mm, "end": v(-15, 104.25) * mm});
            skLineSegment(sketch, "E86", {"start": v(-74.25, 0) * mm, "end": v(74.25, 0) * mm, "construction": true});
            skLineSegment(sketch, "E87.MirrorCS", {"start": v(0, -74.25) * mm, "end": v(0, -104.25) * mm, "construction": true});
            skCircle(sketch, "E88.MirrorC", {"center": v(0, -104.25) * mm, "radius": 6 * mm});
            skLineSegment(sketch, "E89.MirrorCS", {"start": v(-33, -74.25) * mm, "end": v(-15, -92.25) * mm});
            skLineSegment(sketch, "E90.MirrorCS", {"start": v(-15, -92.25) * mm, "end": v(-15, -104.25) * mm});
            skArc(sketch, "E91.MirrorCS", {"start": v(15, -104.25) * mm, "mid": v(0, -119.25) * mm, "end": v(-15, -104.25) * mm});
            skLineSegment(sketch, "E92.MirrorCS", {"start": v(15, -92.25) * mm, "end": v(15, -104.25) * mm});
            skLineSegment(sketch, "E93.MirrorCS", {"start": v(33, -74.25) * mm, "end": v(15, -92.25) * mm});
            skSolve(sketch);
        }
        {
            var Q0;
            Q0=makeQuery(id+"F16.imprint","IMPRINT",FACE,{"disambiguationData":[TD([[makeQuery(id+"F16.imprint","IMPRINT",EDGE,{"derivedFrom":makeQuery(id+"F1.opExtrude","CAP_EDGE",EDGE,{"disambiguationData":[OSD([sQuery(id+"F0.wireOp",EDGE,"E1.left")])],"isStart":true})}),-1.0]])]});
            var Q1;
            Q1=makeQuery(id+"F16.imprint","IMPRINT",FACE,{"disambiguationData":[TD([[makeQuery(id+"F16.imprint","IMPRINT",EDGE,{"derivedFrom":sQuery(id+"F16.wireOp",EDGE,"E88.MirrorC")}),1.0]])]});
            var Q2;
            Q2=makeQuery(id+"F16.imprint","IMPRINT",FACE,{"disambiguationData":[TD([[makeQuery(id+"F16.imprint","IMPRINT",EDGE,{"derivedFrom":sQuery(id+"F16.wireOp",EDGE,"E80")}),-1.0]])]});
            var Q3;
            Q3=makeQuery(id+"F2.opExtrude","CAP_FACE",FACE,{"disambiguationData":[OSD([sQuery(id+"F0.wireOp",EDGE,"E12"),sQuery(id+"F0.wireOp",EDGE,"E13"),sQuery(id+"F0.wireOp",EDGE,"E14"),sQuery(id+"F0.wireOp",EDGE,"E15"),sQuery(id+"F0.wireOp",EDGE,"E17.filletArc"),sQuery(id+"F0.wireOp",EDGE,"E18.filletArc"),sQuery(id+"F0.wireOp",EDGE,"E19.filletArc"),sQuery(id+"F0.wireOp",EDGE,"E20.filletArc"),sQuery(id+"F0.wireOp",EDGE,"E25.0"),sQuery(id+"F0.wireOp",EDGE,"E25.1"),sQuery(id+"F0.wireOp",EDGE,"E25.2"),sQuery(id+"F0.wireOp",EDGE,"E25.3"),sQuery(id+"F0.wireOp",EDGE,"E25.4"),sQuery(id+"F0.wireOp",EDGE,"E25.5"),sQuery(id+"F0.wireOp",EDGE,"E25.6"),sQuery(id+"F0.wireOp",EDGE,"E25.7")])],"isStart":false});
            extrude(context, id + "F17", {"entities" : qUnion([Q0, Q1, Q2]), "operationType" : NewBodyOperationType.ADD, "endBound" : BoundingType.UP_TO_SURFACE, "endBoundEntityFace" : qUnion([Q3]), "depth" : 25 * mm});
        }
    });
